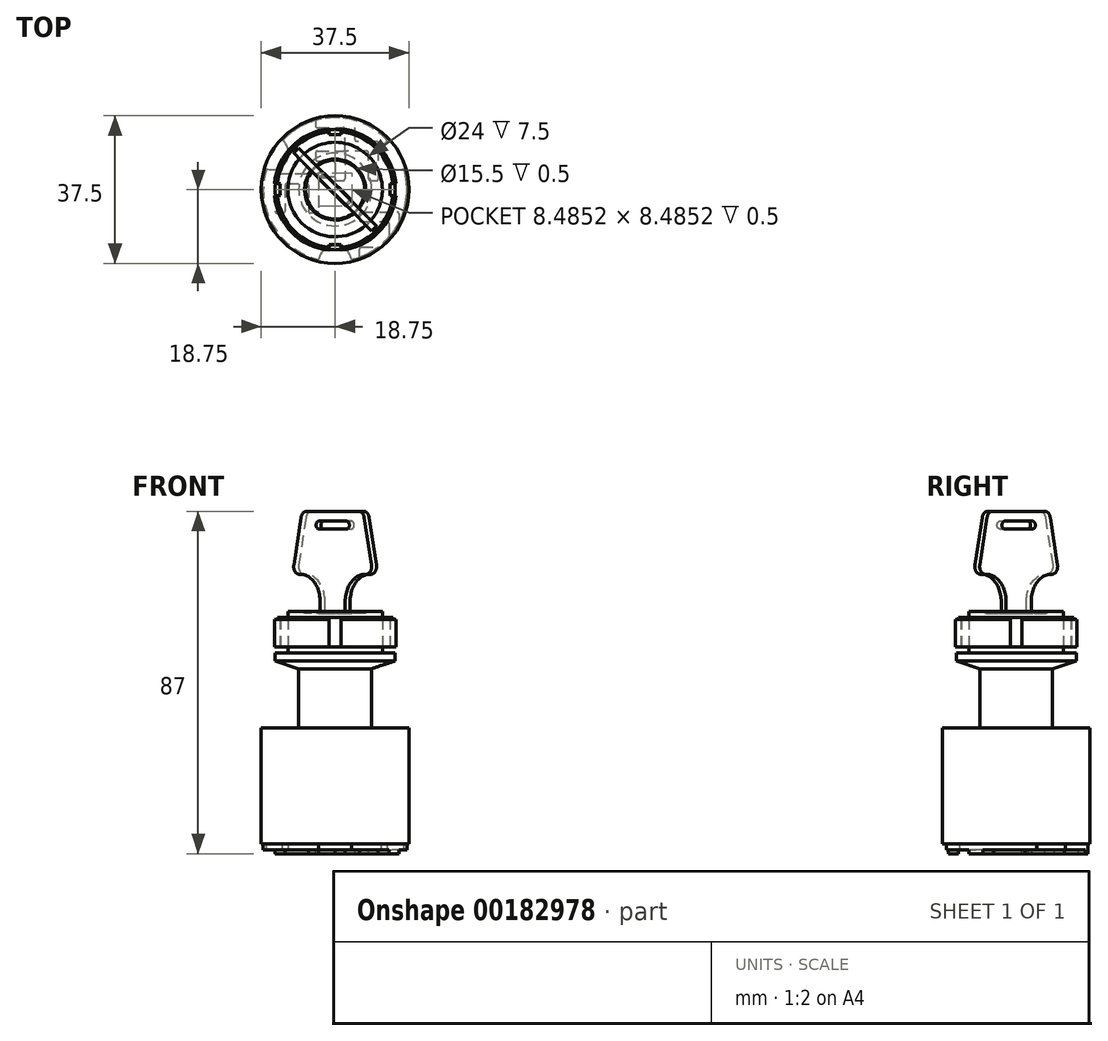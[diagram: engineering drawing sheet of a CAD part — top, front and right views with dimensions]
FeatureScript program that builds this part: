
annotation { "Feature Type Name" : "Feature", "Feature Type Description" : "" }
export const myFeature = defineFeature(function(context is Context, id is Id, definition is map)
    precondition{}
    {
        {
            var Q0;
            Q0=qCreatedBy(makeId("Front.planeOp"),FACE);
            var sketch = newSketch(context, id + "F0", { "sketchPlane" : qUnion([Q0])});
            skLineSegment(sketch, "E0", {"start": v(0, 0) * mm, "end": v(18.75, 0) * mm});
            skLineSegment(sketch, "E1", {"start": v(18.75, 0) * mm, "end": v(18.75, 29.5) * mm});
            skLineSegment(sketch, "E2", {"start": v(9.25, 29.5) * mm, "end": v(9.25, 44.5) * mm});
            skLineSegment(sketch, "E3", {"start": v(9.25, 29.5) * mm, "end": v(18.75, 29.5) * mm});
            skLineSegment(sketch, "E4.0", {"start": v(15.25, 48.5) * mm, "end": v(7.62, 48.5) * mm});
            skLineSegment(sketch, "E5", {"start": v(9.25, 44.5) * mm, "end": v(15.25, 46.5) * mm});
            skLineSegment(sketch, "E6", {"start": v(15.25, 48.5) * mm, "end": v(15.25, 46.5) * mm});
            skLineSegment(sketch, "E7", {"start": v(12, 59) * mm, "end": v(0, 59) * mm});
            skPoint(sketch, "E8.orphan", {"position": v(0, 48.5) * mm});
            skPoint(sketch, "E9.end.orphan", {"position": v(0, 44.5) * mm});
            skLineSegment(sketch, "E10", {"start": v(0, 59) * mm, "end": v(0, 0) * mm});
            skLineSegment(sketch, "E11", {"start": v(12, 59) * mm, "end": v(12, 48.5) * mm});
            skSolve(sketch);
        }
        {
            var Q0;
            Q0 = qSketchRegion(id + "F0", true);
            var Q1;
            Q1=sQuery(id+"F0.wireOp",EDGE,"E10");
            revolve(context, id + "F1", {"entities" : qUnion([Q0]), "axis" : qUnion([Q1]), "revolveType" : RevolveType.FULL});
        }
        {
            var Q0;
            Q0=makeQuery(id+"F1.opRevolve","SWEPT_FACE",FACE,{"disambiguationData":[OSD([sQuery(id+"F0.wireOp",EDGE,"E4.0")])]});
            cPlane(context, id + "F2", {"entities" : qUnion([Q0]), "cplaneType" : CPlaneType.OFFSET, "offset" : 1.5 * mm, "width" : 150 * mm, "height" : 150 * mm});
        }
        {
            var Q0;
            Q0=qCreatedBy(id+"F2.planeOp",FACE);
            var sketch = newSketch(context, id + "F3", { "sketchPlane" : qUnion([Q0])});
            skArc(sketch, "E12", {"start": v(-1.5, 15.43) * mm, "mid": v(-10.96, 10.96) * mm, "end": v(-15.43, 1.5) * mm});
            skCircle(sketch, "E13", {"center": v(0, 0) * mm, "radius": 14 * mm});
            skCircle(sketch, "E14", {"center": v(0, 0) * mm, "radius": 12 * mm});
            skLineSegment(sketch, "E15", {"start": v(0, 14) * mm, "end": v(0, 15.5) * mm});
            skLineSegment(sketch, "E16.0", {"start": v(1.5, 13.92) * mm, "end": v(1.5, 15.43) * mm});
            skLineSegment(sketch, "E17.MirrorCS", {"start": v(-1.5, 13.92) * mm, "end": v(-1.5, 15.43) * mm});
            skLineSegment(sketch, "E18.1.0", {"start": v(-13.92, 1.5) * mm, "end": v(-15.43, 1.5) * mm});
            skLineSegment(sketch, "E18.2.0", {"start": v(-1.5, -13.92) * mm, "end": v(-1.5, -15.43) * mm});
            skLineSegment(sketch, "E18.3.0", {"start": v(13.92, -1.5) * mm, "end": v(15.43, -1.5) * mm});
            skLineSegment(sketch, "E19.1.0", {"start": v(-13.92, -1.5) * mm, "end": v(-15.43, -1.5) * mm});
            skLineSegment(sketch, "E19.2.0", {"start": v(1.5, -13.92) * mm, "end": v(1.5, -15.43) * mm});
            skLineSegment(sketch, "E19.3.0", {"start": v(13.92, 1.5) * mm, "end": v(15.43, 1.5) * mm});
            skArc(sketch, "E20.trimOffspring", {"start": v(15.43, 1.5) * mm, "mid": v(10.96, 10.96) * mm, "end": v(1.5, 15.43) * mm});
            skArc(sketch, "E21.trimOffspring", {"start": v(-15.43, -1.5) * mm, "mid": v(-10.96, -10.96) * mm, "end": v(-1.5, -15.43) * mm});
            skArc(sketch, "E22.trimOffspring", {"start": v(1.5, -15.43) * mm, "mid": v(10.96, -10.96) * mm, "end": v(15.43, -1.5) * mm});
            skSolve(sketch);
        }
        {
            var Q0;
            Q0=makeQuery(id+"F3.imprint","IMPRINT",FACE,{"disambiguationData":[TD([[makeQuery(id+"F3.imprint","IMPRINT",EDGE,{"derivedFrom":sQuery(id+"F3.wireOp",EDGE,"E12")}),1.0]])]});
            var Q1;
            {var subQ0=sQuery(id+"F3.wireOp",EDGE,"E18.2.0");Q1=makeQuery(id+"F3.imprint","IMPRINT",FACE,{"disambiguationData":[TD([[makeQuery(id+"F3.imprint","IMPRINT",EDGE,{"derivedFrom":subQ0}),-1.0]])]});}
            var Q2;
            {var subQ0=sQuery(id+"F3.wireOp",EDGE,"E18.3.0");Q2=makeQuery(id+"F3.imprint","IMPRINT",FACE,{"disambiguationData":[TD([[makeQuery(id+"F3.imprint","IMPRINT",EDGE,{"derivedFrom":subQ0}),-1.0]])]});}
            var Q3;
            Q3=makeQuery(id+"F3.imprint","IMPRINT",FACE,{"disambiguationData":[TD([[makeQuery(id+"F3.imprint","IMPRINT",EDGE,{"derivedFrom":sQuery(id+"F3.wireOp",EDGE,"E14")}),-1.0]])]});
            var Q4;
            {var subQ0=sQuery(id+"F3.wireOp",EDGE,"E16.0");Q4=makeQuery(id+"F3.imprint","IMPRINT",FACE,{"disambiguationData":[TD([[makeQuery(id+"F3.imprint","IMPRINT",EDGE,{"derivedFrom":subQ0}),-1.0]])]});}
            extrude(context, id + "F4", {"entities" : qUnion([Q0, Q1, Q2, Q3, Q4]), "depth" : 7.5 * mm});
        }
        {
            var Q0;
            Q0=makeQuery(id+"F4.opExtrude","CAP_FACE",FACE,{"disambiguationData":[OSD([sQuery(id+"F3.wireOp",EDGE,"E12"),sQuery(id+"F3.wireOp",EDGE,"E13"),sQuery(id+"F3.wireOp",EDGE,"E14"),sQuery(id+"F3.wireOp",EDGE,"E16.0"),sQuery(id+"F3.wireOp",EDGE,"E17.MirrorCS"),sQuery(id+"F3.wireOp",EDGE,"E18.1.0"),sQuery(id+"F3.wireOp",EDGE,"E18.2.0"),sQuery(id+"F3.wireOp",EDGE,"E18.3.0"),sQuery(id+"F3.wireOp",EDGE,"E19.1.0"),sQuery(id+"F3.wireOp",EDGE,"E19.2.0"),sQuery(id+"F3.wireOp",EDGE,"E19.3.0"),sQuery(id+"F3.wireOp",EDGE,"E20.trimOffspring"),sQuery(id+"F3.wireOp",EDGE,"E21.trimOffspring"),sQuery(id+"F3.wireOp",EDGE,"E22.trimOffspring")])],"isStart":false});
            var sketch = newSketch(context, id + "F5", { "sketchPlane" : qUnion([Q0])});
            skCircle(sketch, "E23", {"center": v(0, 0) * mm, "radius": 14.75 * mm});
            skCircle(sketch, "E24", {"center": v(0, 0) * mm, "radius": 15.5 * mm});
            skSolve(sketch);
        }
        {
            var Q0;
            Q0 = qSketchRegion(id + "F5", true);
            extrude(context, id + "F6", {"entities" : qUnion([Q0]), "operationType" : NewBodyOperationType.REMOVE, "oppositeDirection" : true, "depth" : 0.5 * mm});
        }
        {
            var Q0;
            Q0=makeQuery(id+"F1.opRevolve","SWEPT_FACE",FACE,{"disambiguationData":[OSD([sQuery(id+"F0.wireOp",EDGE,"E7")])]});
            var sketch = newSketch(context, id + "F7", { "sketchPlane" : qUnion([Q0])});
            skLineSegment(sketch, "E25", {"start": v(0, 0) * mm, "end": v(0, 4.08) * mm});
            skLineSegment(sketch, "E26.0", {"start": v(-4.24, 2.83) * mm, "end": v(2.83, -4.24) * mm});
            skLineSegment(sketch, "E27.MirrorCS", {"start": v(-2.83, 4.24) * mm, "end": v(4.24, -2.83) * mm});
            skLineSegment(sketch, "E28", {"start": v(2.83, -4.24) * mm, "end": v(4.24, -2.83) * mm});
            skLineSegment(sketch, "E29", {"start": v(-4.24, 2.83) * mm, "end": v(-2.83, 4.24) * mm});
            skCircle(sketch, "E30", {"center": v(0, 0) * mm, "radius": 7.5 * mm});
            skCircle(sketch, "E31", {"center": v(0, 0) * mm, "radius": 7.75 * mm});
            skSolve(sketch);
        }
        {
            var Q0;
            Q0 = qSketchRegion(id + "F7", true);
            var Q1;
            Q1=makeQuery(id+"F7.imprint","IMPRINT",FACE,{"disambiguationData":[TD([[makeQuery(id+"F7.imprint","IMPRINT",EDGE,{"derivedFrom":sQuery(id+"F7.wireOp",EDGE,"E26.0")}),1.0]])]});
            extrude(context, id + "F8", {"entities" : qUnion([Q0, Q1]), "operationType" : NewBodyOperationType.REMOVE, "oppositeDirection" : true, "depth" : 0.5 * mm});
        }
        {
            var Q0;
            Q0=makeQuery(id+"F8.boolean.opBoolean","COPY",FACE,{"derivedFrom":makeQuery(id+"F8.opExtrude","SWEPT_FACE",FACE,{"disambiguationData":[OSD([sQuery(id+"F7.wireOp",EDGE,"E27.MirrorCS")])]})});
            cPlane(context, id + "F9", {"entities" : qUnion([Q0]), "cplaneType" : CPlaneType.OFFSET, "offset" : 1 * mm, "width" : 150 * mm, "height" : 150 * mm});
        }
        {
            var Q0;
            Q0=qCreatedBy(id+"F9.planeOp",FACE);
            var sketch = newSketch(context, id + "F10", { "sketchPlane" : qUnion([Q0])});
            skLineSegment(sketch, "E32", {"start": v(0, 0) * mm, "end": v(0, 58.5) * mm});
            skLineSegment(sketch, "E33", {"start": v(0, 58.5) * mm, "end": v(4.5, 58.5) * mm});
            skLineSegment(sketch, "E34", {"start": v(4.5, 58.5) * mm, "end": v(4.5, 61.5) * mm});
            skLineSegment(sketch, "E35", {"start": v(11.5, 68.5) * mm, "end": v(12.02, 68.5) * mm});
            skPoint(sketch, "E36.visualSharp", {"position": v(4.5, 68.5) * mm});
            skArc(sketch, "E36.filletArc", {"start": v(11.5, 68.5) * mm, "mid": v(6.55, 66.45) * mm, "end": v(4.5, 61.5) * mm});
            skLineSegment(sketch, "E37.0", {"start": v(0, 84.5) * mm, "end": v(9.4, 84.5) * mm});
            skLineSegment(sketch, "E38", {"start": v(11.34, 82.93) * mm, "end": v(13.97, 70.93) * mm});
            skPoint(sketch, "E39.visualSharp", {"position": v(11, 84.5) * mm});
            skArc(sketch, "E39.filletArc", {"start": v(11.34, 82.93) * mm, "mid": v(10.64, 84.06) * mm, "end": v(9.4, 84.5) * mm});
            skPoint(sketch, "E40.visualSharp", {"position": v(14.5, 68.5) * mm});
            skArc(sketch, "E40.filletArc", {"start": v(12.02, 68.5) * mm, "mid": v(13.57, 69.25) * mm, "end": v(13.97, 70.93) * mm});
            skLineSegment(sketch, "E41.MirrorCS", {"start": v(0, 84.5) * mm, "end": v(-9.4, 84.5) * mm});
            skArc(sketch, "E42.MirrorCS", {"start": v(-11.34, 82.93) * mm, "mid": v(-10.64, 84.06) * mm, "end": v(-9.4, 84.5) * mm});
            skLineSegment(sketch, "E43.MirrorCS", {"start": v(-11.34, 82.93) * mm, "end": v(-13.97, 70.93) * mm});
            skArc(sketch, "E44.MirrorCS", {"start": v(-12.02, 68.5) * mm, "mid": v(-13.57, 69.25) * mm, "end": v(-13.97, 70.93) * mm});
            skLineSegment(sketch, "E45.MirrorCS", {"start": v(-11.5, 68.5) * mm, "end": v(-12.02, 68.5) * mm});
            skArc(sketch, "E46.MirrorCS", {"start": v(-11.5, 68.5) * mm, "mid": v(-6.55, 66.45) * mm, "end": v(-4.5, 61.5) * mm});
            skLineSegment(sketch, "E47.MirrorCS", {"start": v(-4.5, 58.5) * mm, "end": v(-4.5, 61.5) * mm});
            skLineSegment(sketch, "E48.MirrorCS", {"start": v(0, 58.5) * mm, "end": v(-4.5, 58.5) * mm});
            skLineSegment(sketch, "E49.0", {"start": v(0, 82) * mm, "end": v(5, 82) * mm});
            skLineSegment(sketch, "E50.0", {"start": v(0, 80) * mm, "end": v(5, 80) * mm});
            skArc(sketch, "E51", {"start": v(5, 80) * mm, "mid": v(6, 81) * mm, "end": v(5, 82) * mm});
            skLineSegment(sketch, "E52.MirrorCS", {"start": v(0, 82) * mm, "end": v(-5, 82) * mm});
            skArc(sketch, "E53.MirrorCS", {"start": v(-5, 80) * mm, "mid": v(-6, 81) * mm, "end": v(-5, 82) * mm});
            skLineSegment(sketch, "E54.MirrorCS", {"start": v(0, 80) * mm, "end": v(-5, 80) * mm});
            skSolve(sketch);
        }
        {
            var Q0;
            Q0=makeQuery(id+"F10.imprint","IMPRINT",FACE,{"disambiguationData":[TD([[makeQuery(id+"F10.imprint","IMPRINT",EDGE,{"derivedFrom":sQuery(id+"F10.wireOp",EDGE,"E33")}),1.0]])]});
            extrude(context, id + "F11", {"entities" : qUnion([Q0]), "endBound" : BoundingType.SYMMETRIC, "depth" : 1.75 * mm});
        }
        {
            var Q0;
            Q0=makeQuery(id+"F1.opRevolve","SWEPT_FACE",FACE,{"disambiguationData":[OSD([sQuery(id+"F0.wireOp",EDGE,"E0")])]});
            var sketch = newSketch(context, id + "F12", { "sketchPlane" : qUnion([Q0])});
            skArc(sketch, "E55", {"start": v(-4.18, 17.76) * mm, "mid": v(0, -18.25) * mm, "end": v(4.18, 17.76) * mm});
            skArc(sketch, "E56", {"start": v(-4.18, 17.76) * mm, "mid": v(0, 14.28) * mm, "end": v(4.18, 17.76) * mm});
            skArc(sketch, "E57.1.0", {"start": v(-13.3, -12.5) * mm, "mid": v(-12.37, -7.14) * mm, "end": v(-17.48, -5.26) * mm});
            skArc(sketch, "E57.2.0", {"start": v(17.48, -5.26) * mm, "mid": v(12.37, -7.14) * mm, "end": v(13.3, -12.5) * mm});
            skSolve(sketch);
        }
        {
            var Q0;
            {var subQ0=sQuery(id+"F12.wireOp",EDGE,"E56");Q0=makeQuery(id+"F12.imprint","IMPRINT",FACE,{"disambiguationData":[TD([[makeQuery(id+"F12.imprint","IMPRINT",EDGE,{"derivedFrom":subQ0}),-1.0]])]});}
            var Q1;
            Q1 = qSketchRegion(id + "F14", true);
            extrude(context, id + "F13", {"entities" : qUnion([Q0, Q1]), "depth" : 1.5 * mm});
        }
        {
            var Q0;
            Q0=makeQuery(id+"F13.opExtrude","CAP_FACE",FACE,{"disambiguationData":[OSD([sQuery(id+"F12.wireOp",EDGE,"E55"),sQuery(id+"F12.wireOp",EDGE,"E56"),sQuery(id+"F12.wireOp",EDGE,"E57.1.0"),sQuery(id+"F12.wireOp",EDGE,"E57.2.0")])],"isStart":false});
            var sketch = newSketch(context, id + "F14", { "sketchPlane" : qUnion([Q0])});
            skSolve(sketch);
        }
        {
            var Q0;
            {var subQ0=sQuery(id+"F12.wireOp",EDGE,"E56");Q0=makeQuery(id+"F14.imprint","IMPRINT",FACE,{"disambiguationData":[TD([[makeQuery(id+"F14.imprint","IMPRINT",EDGE,{"derivedFrom":makeQuery(id+"F13.opExtrude","CAP_EDGE",EDGE,{"disambiguationData":[OSD([subQ0])],"isStart":false})}),-1.0]])]});}
            var sketch = newSketch(context, id + "F15", { "sketchPlane" : qUnion([Q0])});
            skArc(sketch, "E58", {"start": v(-5, -17.55) * mm, "mid": v(0, -18.25) * mm, "end": v(5, -17.55) * mm});
            skLineSegment(sketch, "E59", {"start": v(6.2, 17.17) * mm, "end": v(6.2, 15.17) * mm});
            skLineSegment(sketch, "E60", {"start": v(6.7, 5.67) * mm, "end": v(15.7, 5.67) * mm});
            skLineSegment(sketch, "E61", {"start": v(16.2, 6.17) * mm, "end": v(16.2, 8.41) * mm});
            skLineSegment(sketch, "E62.0", {"start": v(13.7, 8.67) * mm, "end": v(13.7, 12.06) * mm});
            skLineSegment(sketch, "E63.0", {"start": v(6.7, 8.17) * mm, "end": v(13.2, 8.17) * mm});
            skLineSegment(sketch, "E64.0", {"start": v(6.7, 14.67) * mm, "end": v(10.86, 14.67) * mm});
            skLineSegment(sketch, "E65.trimOffspring", {"start": v(6.2, 7.67) * mm, "end": v(6.2, 6.17) * mm});
            skLineSegment(sketch, "E66", {"start": v(-15.25, -3.5) * mm, "end": v(-15.25, 5.5) * mm});
            skLineSegment(sketch, "E67", {"start": v(-14.75, -4) * mm, "end": v(-4.75, -4) * mm});
            skLineSegment(sketch, "E68", {"start": v(-4.25, -3.5) * mm, "end": v(-4.25, -3.15) * mm});
            skLineSegment(sketch, "E69", {"start": v(-4.75, 6) * mm, "end": v(-6.25, 6) * mm});
            skLineSegment(sketch, "E70.1", {"start": v(-6.75, -1) * mm, "end": v(-6.75, 5.5) * mm});
            skLineSegment(sketch, "E70.2", {"start": v(-12.25, -1.5) * mm, "end": v(-7.25, -1.5) * mm});
            skLineSegment(sketch, "E70.3", {"start": v(-12.75, -1) * mm, "end": v(-12.75, 5.5) * mm});
            skLineSegment(sketch, "E71.trimOffspring", {"start": v(-13.25, 6) * mm, "end": v(-14.75, 6) * mm});
            skPoint(sketch, "E72.startSnap0", {"position": v(1.3, -18.25) * mm});
            skLineSegment(sketch, "E73", {"start": v(-5, -17.55) * mm, "end": v(-5, -16.25) * mm});
            skLineSegment(sketch, "E74", {"start": v(-4.5, -7.25) * mm, "end": v(-0.5, -7.25) * mm});
            skLineSegment(sketch, "E75", {"start": v(0, -6.75) * mm, "end": v(0, -3.15) * mm});
            skLineSegment(sketch, "E76", {"start": v(0.5, -2.25) * mm, "end": v(2, -2.25) * mm});
            skLineSegment(sketch, "E77", {"start": v(11, -2.75) * mm, "end": v(11, -11.75) * mm});
            skLineSegment(sketch, "E78", {"start": v(10.5, -12.25) * mm, "end": v(5.5, -12.25) * mm});
            skLineSegment(sketch, "E79", {"start": v(5, -12.75) * mm, "end": v(5, -17.55) * mm});
            skLineSegment(sketch, "E80.0", {"start": v(0, -15.75) * mm, "end": v(-4.5, -15.75) * mm});
            skLineSegment(sketch, "E80.1", {"start": v(8.5, -2.75) * mm, "end": v(8.5, -9.25) * mm});
            skLineSegment(sketch, "E80.2", {"start": v(8, -9.75) * mm, "end": v(3, -9.75) * mm});
            skLineSegment(sketch, "E80.3", {"start": v(2.5, -10.25) * mm, "end": v(2.5, -15.25) * mm});
            skLineSegment(sketch, "E80.4", {"start": v(0, -15.75) * mm, "end": v(2, -15.75) * mm});
            skLineSegment(sketch, "E81.0", {"start": v(2.5, -9.25) * mm, "end": v(2.5, -2.75) * mm});
            skLineSegment(sketch, "E81.1", {"start": v(-4.5, -9.75) * mm, "end": v(2, -9.75) * mm});
            skPoint(sketch, "E82.orphan", {"position": v(16.07, -18.25) * mm});
            skPoint(sketch, "E83.orphan", {"position": v(5, -18.25) * mm});
            skPoint(sketch, "E72.start.orphan", {"position": v(0, -18.25) * mm});
            skLineSegment(sketch, "E84.trimOffspring", {"start": v(-5, -9.25) * mm, "end": v(-5, -7.75) * mm});
            skLineSegment(sketch, "E85.trimOffspring", {"start": v(9, -2.25) * mm, "end": v(10.5, -2.25) * mm});
            skPoint(sketch, "E86.visualSharp", {"position": v(6.2, 14.67) * mm});
            skArc(sketch, "E86.filletArc", {"start": v(6.2, 15.17) * mm, "mid": v(6.34, 14.81) * mm, "end": v(6.7, 14.67) * mm});
            skPoint(sketch, "E87.visualSharp", {"position": v(13.7, 8.17) * mm});
            skArc(sketch, "E87.filletArc", {"start": v(13.2, 8.17) * mm, "mid": v(13.55, 8.31) * mm, "end": v(13.7, 8.67) * mm});
            skPoint(sketch, "E88.visualSharp", {"position": v(6.2, 8.17) * mm});
            skArc(sketch, "E88.filletArc", {"start": v(6.7, 8.17) * mm, "mid": v(6.34, 8.02) * mm, "end": v(6.2, 7.67) * mm});
            skPoint(sketch, "E89.visualSharp", {"position": v(6.2, 5.67) * mm});
            skArc(sketch, "E89.filletArc", {"start": v(6.2, 6.17) * mm, "mid": v(6.34, 5.81) * mm, "end": v(6.7, 5.67) * mm});
            skPoint(sketch, "E90.visualSharp", {"position": v(16.2, 5.67) * mm});
            skArc(sketch, "E90.filletArc", {"start": v(15.7, 5.67) * mm, "mid": v(16.05, 5.81) * mm, "end": v(16.2, 6.17) * mm});
            skPoint(sketch, "E91.visualSharp", {"position": v(-4.25, 6) * mm});
            skArc(sketch, "E91.filletArc", {"start": v(-4.25, 5.5) * mm, "mid": v(-4.4, 5.85) * mm, "end": v(-4.75, 6) * mm});
            skPoint(sketch, "E92.visualSharp", {"position": v(-6.75, 6) * mm});
            skArc(sketch, "E92.filletArc", {"start": v(-6.25, 6) * mm, "mid": v(-6.6, 5.85) * mm, "end": v(-6.75, 5.5) * mm});
            skPoint(sketch, "E93.visualSharp", {"position": v(-12.75, 6) * mm});
            skArc(sketch, "E93.filletArc", {"start": v(-12.75, 5.5) * mm, "mid": v(-12.9, 5.85) * mm, "end": v(-13.25, 6) * mm});
            skPoint(sketch, "E94.visualSharp", {"position": v(-12.75, -1.5) * mm});
            skArc(sketch, "E94.filletArc", {"start": v(-12.75, -1) * mm, "mid": v(-12.6, -1.35) * mm, "end": v(-12.25, -1.5) * mm});
            skPoint(sketch, "E95.visualSharp", {"position": v(-6.75, -1.5) * mm});
            skArc(sketch, "E95.filletArc", {"start": v(-7.25, -1.5) * mm, "mid": v(-6.9, -1.35) * mm, "end": v(-6.75, -1) * mm});
            skPoint(sketch, "E96.visualSharp", {"position": v(-15.25, 6) * mm});
            skArc(sketch, "E96.filletArc", {"start": v(-14.75, 6) * mm, "mid": v(-15.1, 5.85) * mm, "end": v(-15.25, 5.5) * mm});
            skPoint(sketch, "E97.visualSharp", {"position": v(-15.25, -4) * mm});
            skArc(sketch, "E97.filletArc", {"start": v(-15.25, -3.5) * mm, "mid": v(-15.1, -3.85) * mm, "end": v(-14.75, -4) * mm});
            skPoint(sketch, "E98.visualSharp", {"position": v(-4.25, -4) * mm});
            skArc(sketch, "E98.filletArc", {"start": v(-4.75, -4) * mm, "mid": v(-4.4, -3.85) * mm, "end": v(-4.25, -3.5) * mm});
            skPoint(sketch, "E99.visualSharp", {"position": v(0, -2.25) * mm});
            skArc(sketch, "E99.filletArc", {"start": v(0.5, -2.25) * mm, "mid": v(0.15, -2.4) * mm, "end": v(0, -2.75) * mm});
            skPoint(sketch, "E100.visualSharp", {"position": v(2.5, -2.25) * mm});
            skArc(sketch, "E100.filletArc", {"start": v(2.5, -2.75) * mm, "mid": v(2.35, -2.4) * mm, "end": v(2, -2.25) * mm});
            skPoint(sketch, "E101.visualSharp", {"position": v(8.5, -2.25) * mm});
            skArc(sketch, "E101.filletArc", {"start": v(9, -2.25) * mm, "mid": v(8.65, -2.4) * mm, "end": v(8.5, -2.75) * mm});
            skPoint(sketch, "E102.visualSharp", {"position": v(11, -2.25) * mm});
            skArc(sketch, "E102.filletArc", {"start": v(11, -2.75) * mm, "mid": v(10.85, -2.4) * mm, "end": v(10.5, -2.25) * mm});
            skPoint(sketch, "E103.visualSharp", {"position": v(0, -7.25) * mm});
            skArc(sketch, "E103.filletArc", {"start": v(-0.5, -7.25) * mm, "mid": v(-0.15, -7.1) * mm, "end": v(0, -6.75) * mm});
            skPoint(sketch, "E104.visualSharp", {"position": v(-5, -7.25) * mm});
            skArc(sketch, "E104.filletArc", {"start": v(-4.5, -7.25) * mm, "mid": v(-4.85, -7.4) * mm, "end": v(-5, -7.75) * mm});
            skPoint(sketch, "E105.visualSharp", {"position": v(-5, -9.75) * mm});
            skArc(sketch, "E105.filletArc", {"start": v(-5, -9.25) * mm, "mid": v(-4.85, -9.6) * mm, "end": v(-4.5, -9.75) * mm});
            skPoint(sketch, "E106.visualSharp", {"position": v(8.5, -9.75) * mm});
            skArc(sketch, "E106.filletArc", {"start": v(8, -9.75) * mm, "mid": v(8.35, -9.6) * mm, "end": v(8.5, -9.25) * mm});
            skPoint(sketch, "E107.visualSharp", {"position": v(11, -12.25) * mm});
            skArc(sketch, "E107.filletArc", {"start": v(10.5, -12.25) * mm, "mid": v(10.85, -12.1) * mm, "end": v(11, -11.75) * mm});
            skPoint(sketch, "E108.visualSharp", {"position": v(5, -12.25) * mm});
            skArc(sketch, "E108.filletArc", {"start": v(5.5, -12.25) * mm, "mid": v(5.15, -12.4) * mm, "end": v(5, -12.75) * mm});
            skPoint(sketch, "E109.visualSharp", {"position": v(2.5, -15.75) * mm});
            skArc(sketch, "E109.filletArc", {"start": v(2, -15.75) * mm, "mid": v(2.35, -15.6) * mm, "end": v(2.5, -15.25) * mm});
            skPoint(sketch, "E110.visualSharp", {"position": v(-5, -15.75) * mm});
            skArc(sketch, "E110.filletArc", {"start": v(-4.5, -15.75) * mm, "mid": v(-4.85, -15.9) * mm, "end": v(-5, -16.25) * mm});
            skArc(sketch, "E111.trimOffspring", {"start": v(10.86, 14.67) * mm, "mid": v(8.62, 16.09) * mm, "end": v(6.2, 17.17) * mm});
            skArc(sketch, "E112.trimOffspring", {"start": v(16.2, 8.41) * mm, "mid": v(15.06, 10.32) * mm, "end": v(13.7, 12.06) * mm});
            skCircle(sketch, "E113", {"center": v(0, 0) * mm, "radius": 18.25 * mm});
            skPoint(sketch, "E114.startSnap0", {"position": v(-12.75, 2.25) * mm});
            skPoint(sketch, "E115.visualSharp", {"position": v(2.5, -9.75) * mm});
            skArc(sketch, "E115.filletArc", {"start": v(2.5, -9.25) * mm, "mid": v(2.65, -9.6) * mm, "end": v(3, -9.75) * mm});
            skArc(sketch, "E116.filletArc", {"start": v(2.5, -10.25) * mm, "mid": v(2.35, -9.9) * mm, "end": v(2, -9.75) * mm});
            skPoint(sketch, "E114.start.orphan", {"position": v(-15.25, 2.25) * mm});
            skLineSegment(sketch, "E117", {"start": v(0, -3.15) * mm, "end": v(-4.25, -3.15) * mm});
            skLineSegment(sketch, "E118", {"start": v(-4.25, -3.03) * mm, "end": v(0, -3.03) * mm});
            skLineSegment(sketch, "E119.trimOffspring", {"start": v(0, -3.03) * mm, "end": v(0, -2.75) * mm});
            skLineSegment(sketch, "E120.trimOffspring", {"start": v(-4.25, -3.03) * mm, "end": v(-4.25, 5.5) * mm});
            skSolve(sketch);
        }
        {
            var Q0;
            {var subQ1=sQuery(id+"F15.wireOp",EDGE,"E73");Q0=makeQuery(id+"F15.imprint","IMPRINT",FACE,{"disambiguationData":[TD([[makeQuery(id+"F15.imprint","IMPRINT",EDGE,{"derivedFrom":subQ1}),-1.0]])]});}
            extrude(context, id + "F16", {"entities" : qUnion([Q0]), "operationType" : NewBodyOperationType.ADD, "depth" : 1 * mm});
        }
        {
            var Q0;
            {var subQ0=sQuery(id+"F15.wireOp",EDGE,"E59");Q0=makeQuery(id+"F15.imprint","IMPRINT",FACE,{"disambiguationData":[TD([[makeQuery(id+"F15.imprint","IMPRINT",EDGE,{"derivedFrom":subQ0}),1.0]])]});}
            extrude(context, id + "F17", {"entities" : qUnion([Q0]), "depth" : 1 * mm});
        }
        {
            var Q0;
            Q0=makeQuery(id+"F15.imprint","IMPRINT",FACE,{"disambiguationData":[TD([[makeQuery(id+"F15.imprint","IMPRINT",EDGE,{"derivedFrom":sQuery(id+"F15.wireOp",EDGE,"E60")}),1.0]])]});
            extrude(context, id + "F18", {"entities" : qUnion([Q0]), "operationType" : NewBodyOperationType.ADD, "depth" : 1 * mm});
        }
    });
